# Revit family: SWRS70X360
name_source: partatom
category: Structural Connections
revit_build: Autodesk Revit 2015 (Build: 20140606_1530(x64)
units: mm (PartAtom-declared; Revit-internal decimal feet)

## types (1)
- SWRS70X360
    Default Elevation = 0 mm  [stored 0 ft]
    Density = 0.06 kg
    Description = Screws
    EPD = https://www.strongtie.eu
    ETA / DoP = https://www.strongtie.eu
    Manufacturer = Simpson Strong-Tie
    Model = SWRS7.0X360
    Model Disclaimer = Contact Simpson Strong-Tie Company  for more information
    Model ID = 0303012525179226512283611868705725076737
    Name = SWRS7.0X360
    ObjectType = SWRS7.0X360
    Product Material = Supracoat 2C Steel
    Product Type = Screws
    Reference = 77931
    Technical datasheet = https://www.strongtie.eu
    URL = www.strongtie.eu
    UniClass Number = Pr_20_29_76_98
    UniClass Title = Wood screws

note: [stored X ft] marks values corroborated as IEEE doubles in the binary element streams (Revit-internal decimal feet)

## geometry (parser evidence)
native form markers: Blend x31, Sweep x3
no freeform markers — native parametric forms only
